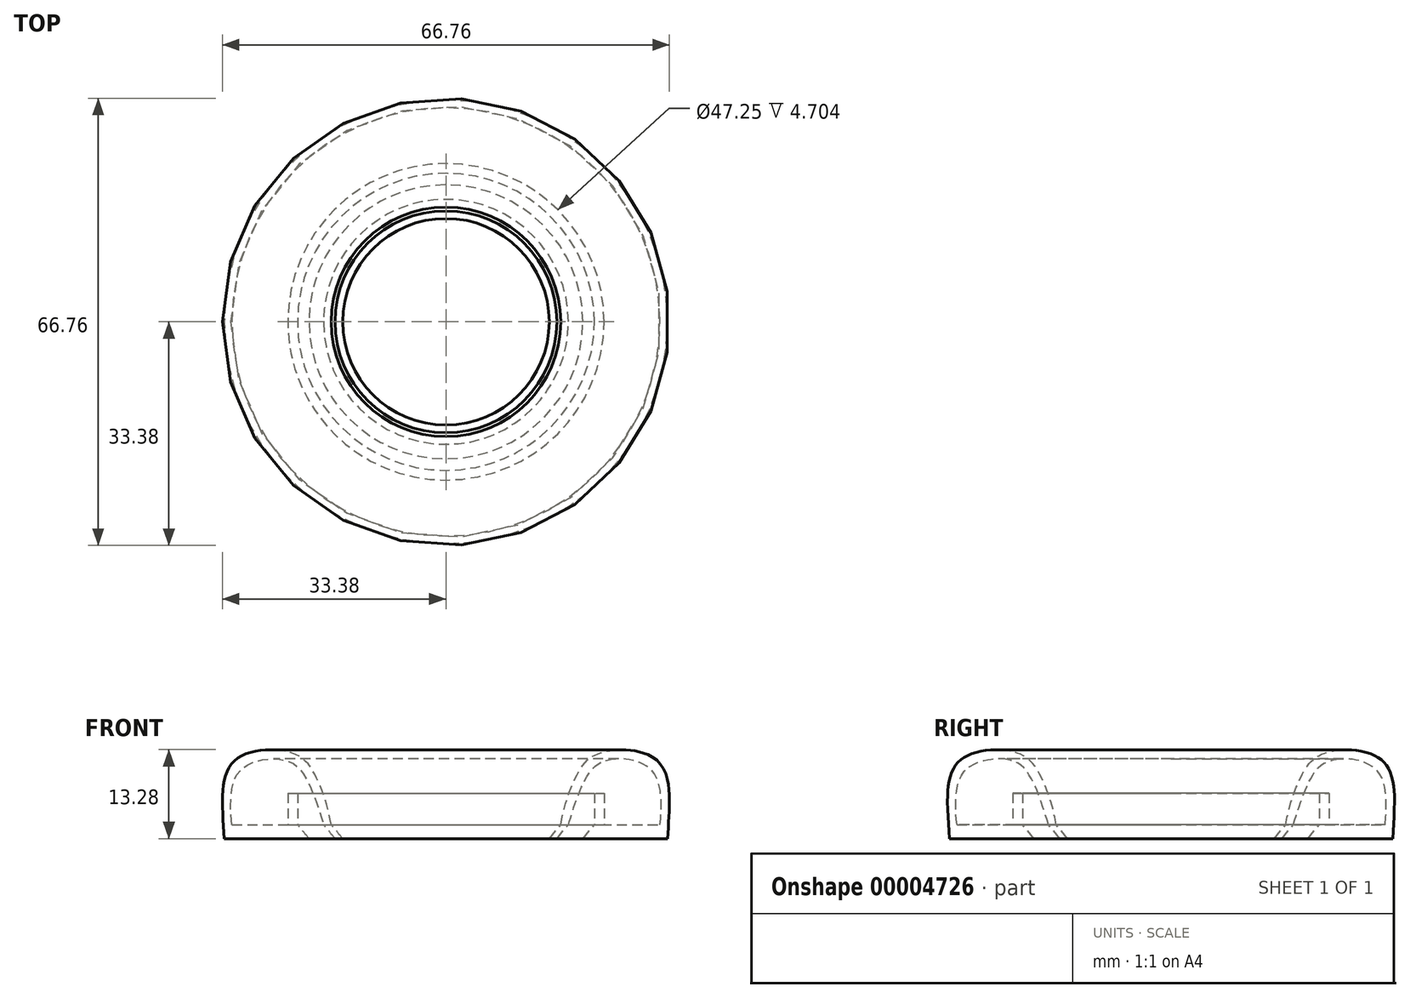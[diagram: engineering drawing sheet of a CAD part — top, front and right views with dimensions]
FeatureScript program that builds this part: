
annotation { "Feature Type Name" : "Feature", "Feature Type Description" : "" }
export const myFeature = defineFeature(function(context is Context, id is Id, definition is map)
    precondition{}
    {
        {
            var Q0;
            Q0=qCreatedBy(makeId("Right.planeOp"),FACE);
            var sketch = newSketch(context, id + "F0", { "sketchPlane" : qUnion([Q0])});
            skLineSegment(sketch, "E0", {"start": v(-33.1, 0) * mm, "end": v(-20.45, 0) * mm});
            skLineSegment(sketch, "E1", {"start": v(0, 12.83) * mm, "end": v(0, 0) * mm});
            skLineSegment(sketch, "E2", {"start": v(-18.28, 2.1) * mm, "end": v(-16.57, 0) * mm});
            skLineSegment(sketch, "E3", {"start": v(-20.45, 0) * mm, "end": v(-22.17, 2.1) * mm});
            skLineSegment(sketch, "E4", {"start": v(-22.17, 2.1) * mm, "end": v(-22.17, 6.8) * mm});
            skLineSegment(sketch, "E5", {"start": v(-22.17, 6.8) * mm, "end": v(-23.62, 6.8) * mm});
            skLineSegment(sketch, "E6", {"start": v(-23.62, 6.8) * mm, "end": v(-23.62, 2.1) * mm});
            skLineSegment(sketch, "E7", {"start": v(-23.62, 2.1) * mm, "end": v(-31.96, 2.1) * mm});
            skLineSegment(sketch, "E8", {"start": v(-16.57, 0) * mm, "end": v(-15.43, 0) * mm});
            skLineSegment(sketch, "E9", {"start": v(-15.43, 0) * mm, "end": v(-17.14, 2.1) * mm});
            skFitSpline(sketch, "E10", {"points": [v(-17.14, 2.1) * mm, v(-19.47, 9.34) * mm, v(-23, 12.8) * mm, v(-31.68, 11.53) * mm, v(-33.1, 0) * mm], "startDerivative": vector(-5.79, 33.67) * mm, "endDerivative": vector(2.6, -47.52) * mm});
            skFitSpline(sketch, "E11", {"points": [v(-31.96, 2.1) * mm, v(-32, 7.12) * mm, v(-30.77, 10.15) * mm, v(-27.28, 11.8) * mm, v(-23.26, 11.45) * mm, v(-21.04, 9.27) * mm, v(-19.35, 5.36) * mm, v(-18.28, 2.1) * mm], "startDerivative": vector(-4.7, 32.74) * mm, "endDerivative": vector(7.38, -23.71) * mm});
            skSolve(sketch);
        }
        {
            var Q0;
            Q0=sQuery(id+"F0.wireOp",EDGE,"E11");
            var Q1;
            Q1=sQuery(id+"F0.wireOp",EDGE,"E9");
            var Q2;
            Q2=sQuery(id+"F0.wireOp",EDGE,"E4");
            var Q3;
            Q3=sQuery(id+"F0.wireOp",EDGE,"E7");
            var Q4;
            Q4=sQuery(id+"F0.wireOp",EDGE,"E2");
            var Q5;
            Q5=sQuery(id+"F0.wireOp",EDGE,"E6");
            var Q6;
            Q6=sQuery(id+"F0.wireOp",EDGE,"E5");
            var Q7;
            Q7=sQuery(id+"F0.wireOp",EDGE,"E3");
            var Q8;
            Q8=sQuery(id+"F0.wireOp",EDGE,"E8");
            var Q9;
            Q9=sQuery(id+"F0.wireOp",EDGE,"E10");
            var Q10;
            Q10=sQuery(id+"F0.wireOp",EDGE,"E0");
            var Q11;
            Q11=sQuery(id+"F0.wireOp",EDGE,"E1");
            revolve(context, id + "F1", {"bodyType" : ToolBodyType.SURFACE, "surfaceEntities" : qUnion([Q0, Q1, Q2, Q3, Q4, Q5, Q6, Q7, Q8, Q9, Q10]), "axis" : qUnion([Q11]), "revolveType" : RevolveType.FULL});
        }
    });
